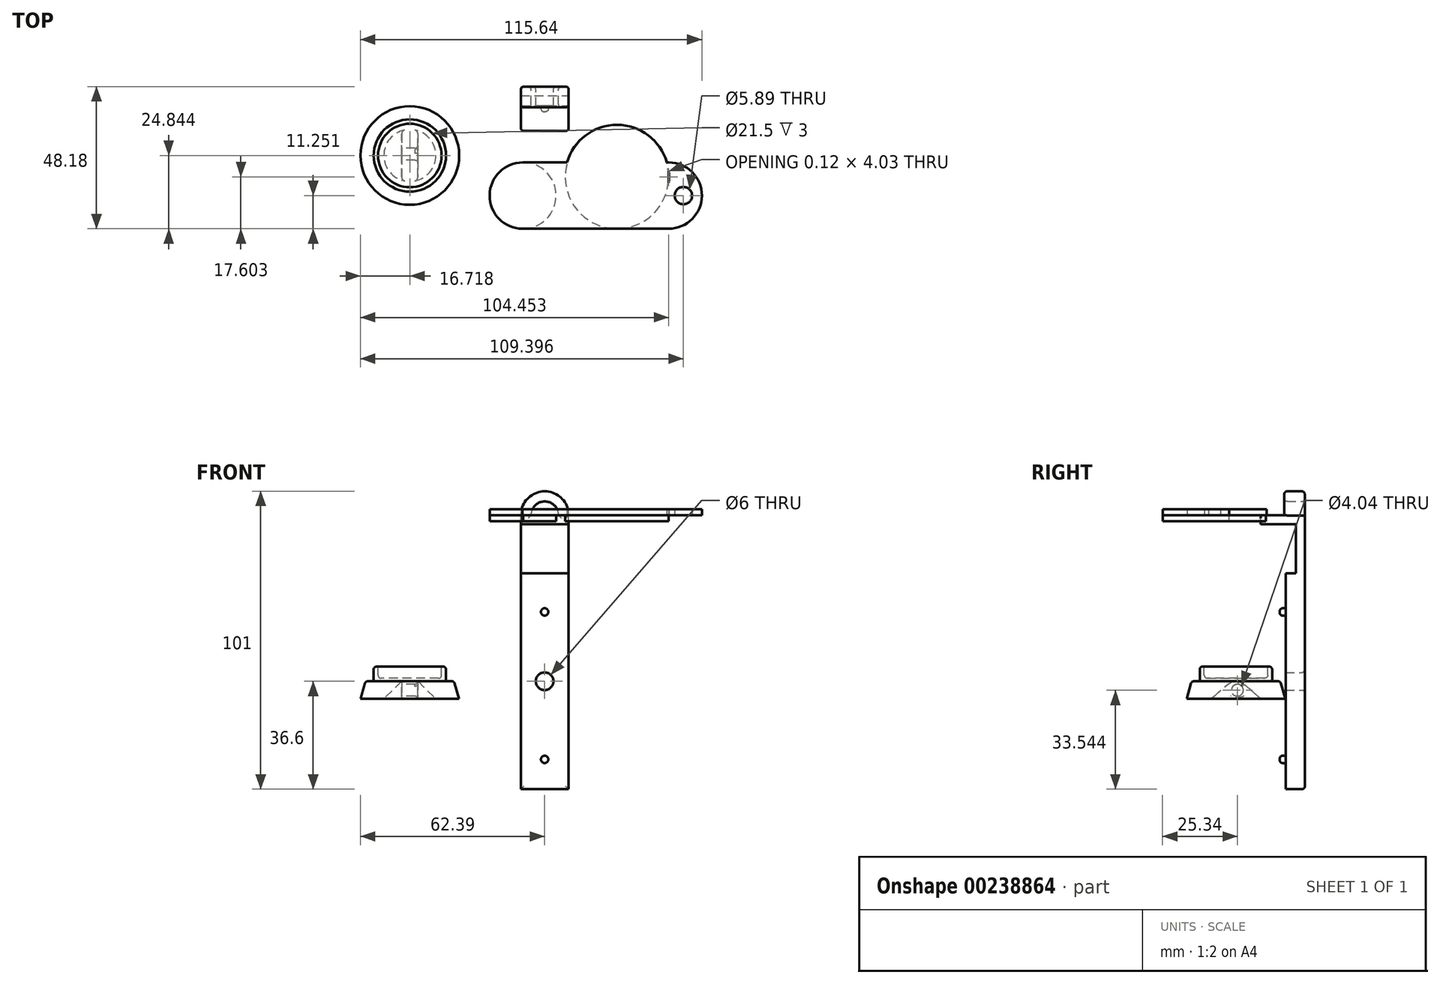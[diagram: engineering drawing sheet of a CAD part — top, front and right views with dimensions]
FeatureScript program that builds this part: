
annotation { "Feature Type Name" : "Feature", "Feature Type Description" : "" }
export const myFeature = defineFeature(function(context is Context, id is Id, definition is map)
    precondition{}
    {
        {
            var Q0;
            Q0=qCreatedBy(makeId("Front.planeOp"),FACE);
            var sketch = newSketch(context, id + "F0", { "sketchPlane" : qUnion([Q0])});
            skCircle(sketch, "E0", {"center": v(0, 0) * mm, "radius": 3 * mm});
            skLineSegment(sketch, "E1", {"start": v(0, 0) * mm, "end": v(0, 36.5) * mm});
            skCircle(sketch, "E2", {"center": v(0, 0) * mm, "radius": 8.06 * mm});
            skLineSegment(sketch, "E3.bottom", {"start": v(-8.06, 0) * mm, "end": v(8.14, 0) * mm});
            skLineSegment(sketch, "E3.top", {"start": v(-8.06, 36.6) * mm, "end": v(8.14, 36.6) * mm});
            skLineSegment(sketch, "E3.left", {"start": v(-8.06, 0) * mm, "end": v(-8.06, 36.6) * mm});
            skLineSegment(sketch, "E3.right", {"start": v(8.14, 0) * mm, "end": v(8.14, 36.6) * mm});
            skLineSegment(sketch, "E4.MirrorCS", {"start": v(8.14, 0) * mm, "end": v(8.14, -36.6) * mm});
            skLineSegment(sketch, "E5.MirrorCS", {"start": v(-8.06, -36.6) * mm, "end": v(8.14, -36.6) * mm});
            skLineSegment(sketch, "E6.MirrorCS", {"start": v(-8.06, 0) * mm, "end": v(-8.06, -36.6) * mm});
            skSolve(sketch);
        }
        {
            var Q0;
            Q0=makeQuery(id+"F0.imprint","IMPRINT",FACE,{"disambiguationData":[TD([[makeQuery(id+"F0.imprint","IMPRINT",EDGE,{"derivedFrom":sQuery(id+"F0.wireOp",EDGE,"E3.top")}),-1.0]])]});
            var Q1;
            {var subQ0=sQuery(id+"F0.wireOp",EDGE,"E1");var subQ1=sQuery(id+"F0.wireOp",EDGE,"E0");var subQ2=makeQuery(id+"F0.imprint","INTERSECT",VERTEX,{"derivedFrom":[subQ1,subQ0]});Q1=makeQuery(id+"F0.imprint","IMPRINT",FACE,{"disambiguationData":[TD([[makeQuery(id+"F0.imprint","IMPRINT",EDGE,{"disambiguationData":[TD([[subQ2,-1.0]])],"derivedFrom":subQ1}),-1.0]])]});}
            var Q2;
            {var subQ0=sQuery(id+"F0.wireOp",EDGE,"E1");var subQ1=sQuery(id+"F0.wireOp",EDGE,"E0");var subQ2=makeQuery(id+"F0.imprint","INTERSECT",VERTEX,{"derivedFrom":[subQ1,subQ0]});Q2=makeQuery(id+"F0.imprint","IMPRINT",FACE,{"disambiguationData":[TD([[makeQuery(id+"F0.imprint","IMPRINT",EDGE,{"disambiguationData":[TD([[subQ2,1.0]])],"derivedFrom":subQ1}),-1.0]])]});}
            var Q3;
            {var subQ0=sQuery(id+"F0.wireOp",EDGE,"E3.bottom");var subQ1=sQuery(id+"F0.wireOp",EDGE,"E0");var subQ2=makeQuery(id+"F0.imprint","INTERSECT",VERTEX,{"disambiguationData":[OD(0.0)],"derivedFrom":[subQ1,subQ0]});Q3=makeQuery(id+"F0.imprint","IMPRINT",FACE,{"disambiguationData":[TD([[makeQuery(id+"F0.imprint","IMPRINT",EDGE,{"disambiguationData":[TD([[subQ2,1.0]])],"derivedFrom":subQ1}),-1.0]])]});}
            var Q4;
            {var subQ0=sQuery(id+"F0.wireOp",EDGE,"E4.MirrorCS");Q4=makeQuery(id+"F0.imprint","IMPRINT",FACE,{"disambiguationData":[TD([[makeQuery(id+"F0.imprint","IMPRINT",EDGE,{"derivedFrom":subQ0}),-1.0]])]});}
            extrude(context, id + "F1", {"entities" : qUnion([Q0, Q1, Q2, Q3, Q4]), "depth" : 3.5 * mm});
        }
        {
            var Q0;
            Q0=makeQuery(id+"F1.opExtrude","CAP_FACE",FACE,{"disambiguationData":[OSD([sQuery(id+"F0.wireOp",EDGE,"E0"),sQuery(id+"F0.wireOp",EDGE,"E2"),sQuery(id+"F0.wireOp",EDGE,"E3.bottom"),sQuery(id+"F0.wireOp",EDGE,"E3.top"),sQuery(id+"F0.wireOp",EDGE,"E3.left"),sQuery(id+"F0.wireOp",EDGE,"E3.right")])],"isStart":false});
            var sketch = newSketch(context, id + "F2", { "sketchPlane" : qUnion([Q0])});
            skLineSegment(sketch, "E7", {"start": v(0, 0) * mm, "end": v(0, 23.5) * mm});
            skCircle(sketch, "E8", {"center": v(0, 23.5) * mm, "radius": 1.25 * mm});
            skLineSegment(sketch, "E9", {"start": v(-5.3, 0) * mm, "end": v(-5.3, -26.5) * mm});
            skCircle(sketch, "E10", {"center": v(0, -26.5) * mm, "radius": 1.24 * mm});
            skSolve(sketch);
        }
        {
            var Q0;
            Q0=makeQuery(id+"F2.imprint","IMPRINT",FACE,{"disambiguationData":[TD([[makeQuery(id+"F2.imprint","IMPRINT",EDGE,{"derivedFrom":sQuery(id+"F2.wireOp",EDGE,"E8")}),1.0]])]});
            var Q1;
            Q1=makeQuery(id+"F2.imprint","IMPRINT",FACE,{"disambiguationData":[TD([[makeQuery(id+"F2.imprint","IMPRINT",EDGE,{"derivedFrom":sQuery(id+"F2.wireOp",EDGE,"E10")}),1.0]])]});
            extrude(context, id + "F3", {"entities" : qUnion([Q0, Q1]), "operationType" : NewBodyOperationType.ADD, "depth" : 2 * mm});
        }
        {
            var Q0;
            Q0=makeQuery(id+"F1.opExtrude","CAP_FACE",FACE,{"disambiguationData":[OSD([sQuery(id+"F0.wireOp",EDGE,"E0"),sQuery(id+"F0.wireOp",EDGE,"E2"),sQuery(id+"F0.wireOp",EDGE,"E3.bottom"),sQuery(id+"F0.wireOp",EDGE,"E3.top"),sQuery(id+"F0.wireOp",EDGE,"E3.left"),sQuery(id+"F0.wireOp",EDGE,"E3.right")])],"isStart":true});
            extrude(context, id + "F4", {"entities" : qUnion([Q0]), "operationType" : NewBodyOperationType.ADD, "depth" : 3 * mm});
        }
        {
            var Q0;
            {var subQ0=sQuery(id+"F0.wireOp",EDGE,"E3.top");Q0=makeQuery(id+"F4.boolean.opBoolean","MERGE",FACE,{"derivedFrom":[makeQuery(id+"F1.opExtrude","SWEPT_FACE",FACE,{"disambiguationData":[OSD([subQ0])]}),makeQuery(id+"F4.opExtrude","SWEPT_FACE",FACE,{"disambiguationData":[OSD([subQ0])]})]});}
            var sketch = newSketch(context, id + "F5", { "sketchPlane" : qUnion([Q0])});
            skLineSegment(sketch, "E11.bottom", {"start": v(-8.06, 3) * mm, "end": v(8.14, 3) * mm});
            skLineSegment(sketch, "E11.top", {"start": v(-8.06, 0) * mm, "end": v(8.14, 0) * mm});
            skLineSegment(sketch, "E11.left", {"start": v(-8.06, 3) * mm, "end": v(-8.06, 0) * mm});
            skLineSegment(sketch, "E11.right", {"start": v(8.14, 3) * mm, "end": v(8.14, 0) * mm});
            skSolve(sketch);
        }
        {
            var Q0;
            Q0=makeQuery(id+"F5.imprint","IMPRINT",FACE,{"disambiguationData":[TD([[makeQuery(id+"F5.imprint","IMPRINT",EDGE,{"derivedFrom":sQuery(id+"F5.wireOp",EDGE,"E11.bottom")}),-1.0]])]});
            extrude(context, id + "F6", {"entities" : qUnion([Q0]), "operationType" : NewBodyOperationType.ADD, "depth" : 16.7 * mm});
        }
        {
            var Q0;
            {var subQ0=sQuery(id+"F0.wireOp",EDGE,"E3.right");Q0=makeQuery(id+"F6.boolean.opBoolean","MERGE",FACE,{"derivedFrom":[makeQuery(id+"F4.boolean.opBoolean","MERGE",FACE,{"derivedFrom":[makeQuery(id+"F1.opExtrude","SWEPT_FACE",FACE,{"disambiguationData":[OSD([subQ0])]}),makeQuery(id+"F4.opExtrude","SWEPT_FACE",FACE,{"disambiguationData":[OSD([subQ0])]})]}),makeQuery(id+"F6.opExtrude","SWEPT_FACE",FACE,{"disambiguationData":[OSD([sQuery(id+"F5.wireOp",EDGE,"E11.right")])]})]});}
            var sketch = newSketch(context, id + "F7", { "sketchPlane" : qUnion([Q0])});
            skLineSegment(sketch, "E12.bottom", {"start": v(3, 53.3) * mm, "end": v(-12, 53.3) * mm});
            skLineSegment(sketch, "E12.top", {"start": v(3, 56.3) * mm, "end": v(-12, 56.3) * mm});
            skLineSegment(sketch, "E12.left", {"start": v(3, 53.3) * mm, "end": v(3, 56.3) * mm});
            skLineSegment(sketch, "E12.right", {"start": v(-12, 53.3) * mm, "end": v(-12, 56.3) * mm});
            skSolve(sketch);
        }
        {
            var Q0;
            Q0=makeQuery(id+"F7.imprint","IMPRINT",FACE,{"disambiguationData":[TD([[makeQuery(id+"F7.imprint","IMPRINT",EDGE,{"derivedFrom":sQuery(id+"F7.wireOp",EDGE,"E12.top")}),1.0]])]});
            extrude(context, id + "F8", {"entities" : qUnion([Q0]), "operationType" : NewBodyOperationType.ADD, "oppositeDirection" : true, "depth" : 16.2 * mm});
        }
        {
            var Q0;
            Q0=makeQuery(id+"F8.boolean.opBoolean","MERGE",FACE,{"derivedFrom":[makeQuery(id+"F6.boolean.opBoolean","MERGE",FACE,{"derivedFrom":[makeQuery(id+"F4.opExtrude","CAP_FACE",FACE,{"disambiguationData":[OSD([sQuery(id+"F0.wireOp",EDGE,"E0"),sQuery(id+"F0.wireOp",EDGE,"E3.top"),sQuery(id+"F0.wireOp",EDGE,"E3.left"),sQuery(id+"F0.wireOp",EDGE,"E3.right"),sQuery(id+"F0.wireOp",EDGE,"E4.MirrorCS"),sQuery(id+"F0.wireOp",EDGE,"E5.MirrorCS"),sQuery(id+"F0.wireOp",EDGE,"E6.MirrorCS")])],"isStart":false}),makeQuery(id+"F6.opExtrude","SWEPT_FACE",FACE,{"disambiguationData":[OSD([sQuery(id+"F5.wireOp",EDGE,"E11.bottom")])]})]}),makeQuery(id+"F8.opExtrude","SWEPT_FACE",FACE,{"disambiguationData":[OSD([sQuery(id+"F7.wireOp",EDGE,"E12.left")])]})]});
            var sketch = newSketch(context, id + "F9", { "sketchPlane" : qUnion([Q0])});
            skCircle(sketch, "E13", {"center": v(-0.04, 56.3) * mm, "radius": 8.1 * mm});
            skCircle(sketch, "E14", {"center": v(-0.04, 56.3) * mm, "radius": 4.66 * mm});
            skSolve(sketch);
        }
        {
            var Q0;
            {var subQ0=sQuery(id+"F7.wireOp",EDGE,"E12.left");var subQ1=makeQuery(id+"F8.opExtrude","CAP_EDGE",EDGE,{"disambiguationData":[OSD([subQ0])],"isStart":false});var subQ9=sQuery(id+"F9.wireOp",EDGE,"E13");var subQ11=makeQuery(id+"F9.imprint","INTERSECT",VERTEX,{"derivedFrom":[subQ1,subQ9]});Q0=makeQuery(id+"F9.imprint","IMPRINT",FACE,{"disambiguationData":[TD([[makeQuery(id+"F9.imprint","IMPRINT",EDGE,{"disambiguationData":[TD([[subQ11,-1.0]])],"derivedFrom":subQ1}),-1.0]])]});}
            extrude(context, id + "F10", {"entities" : qUnion([Q0]), "operationType" : NewBodyOperationType.ADD, "oppositeDirection" : true, "depth" : 7 * mm});
        }
        {
            var Q0;
            Q0=makeQuery(id+"F8.opExtrude","SWEPT_FACE",FACE,{"disambiguationData":[OSD([sQuery(id+"F7.wireOp",EDGE,"E12.top")])]});
            var sketch = newSketch(context, id + "F11", { "sketchPlane" : qUnion([Q0])});
            skCircle(sketch, "E15", {"center": v(24.5, -27.68) * mm, "radius": 17.5 * mm});
            skLineSegment(sketch, "E16", {"start": v(24.5, -45.18) * mm, "end": v(-7.5, -45.18) * mm});
            skCircle(sketch, "E17", {"center": v(-7.38, -33.93) * mm, "radius": 11.25 * mm});
            skPoint(sketch, "E17.second.point", {"position": v(-7.5, -22.68) * mm});
            skPoint(sketch, "E17.third.point", {"position": v(3.87, -33.79) * mm});
            skSolve(sketch);
        }
        {
            var Q0;
            {var subQ0=sQuery(id+"F11.wireOp",EDGE,"E17");var subQ1=sQuery(id+"F11.wireOp",EDGE,"E16");var subQ2=makeQuery(id+"F11.imprint","INTERSECT",VERTEX,{"disambiguationData":[OD(0.0)],"derivedFrom":[subQ1,subQ0]});Q0=makeQuery(id+"F11.imprint","IMPRINT",FACE,{"disambiguationData":[TD([[makeQuery(id+"F11.imprint","IMPRINT",EDGE,{"disambiguationData":[TD([[subQ2,1.0]])],"derivedFrom":subQ1}),-1.0]])]});}
            var Q1;
            Q1=makeQuery(id+"F11.imprint","IMPRINT",FACE,{"disambiguationData":[TD([[makeQuery(id+"F11.imprint","IMPRINT",EDGE,{"derivedFrom":sQuery(id+"F11.wireOp",EDGE,"E15")}),1.0]])]});
            extrude(context, id + "F12", {"entities" : qUnion([Q0, Q1]), "oppositeDirection" : true, "depth" : 2 * mm});
        }
        {
            var Q0;
            Q0=makeQuery(id+"F12.opExtrude","CAP_FACE",FACE,{"disambiguationData":[OSD([sQuery(id+"F11.wireOp",EDGE,"E16"),sQuery(id+"F11.wireOp",EDGE,"E17")])],"isStart":true});
            var sketch = newSketch(context, id + "F13", { "sketchPlane" : qUnion([Q0])});
            skLineSegment(sketch, "E18.bottom", {"start": v(-7.38, -22.68) * mm, "end": v(25.1, -22.68) * mm});
            skLineSegment(sketch, "E18.top", {"start": v(-7.38, -45.18) * mm, "end": v(25.1, -45.18) * mm});
            skLineSegment(sketch, "E18.left", {"start": v(-7.38, -22.68) * mm, "end": v(-7.38, -45.18) * mm});
            skLineSegment(sketch, "E18.right", {"start": v(25.1, -22.68) * mm, "end": v(25.1, -45.18) * mm});
            skCircle(sketch, "E19", {"center": v(24.5, -27.58) * mm, "radius": 17.61 * mm});
            skPoint(sketch, "E19.first.point", {"position": v(22.08, -10.13) * mm});
            skPoint(sketch, "E19.third.point", {"position": v(42.05, -29.2) * mm});
            skLineSegment(sketch, "E20.bottom", {"start": v(25.1, -22.68) * mm, "end": v(42, -22.68) * mm});
            skLineSegment(sketch, "E20.top", {"start": v(25.1, -45.18) * mm, "end": v(42, -45.18) * mm});
            skLineSegment(sketch, "E20.right", {"start": v(42, -22.68) * mm, "end": v(42, -45.18) * mm});
            skArc(sketch, "E21", {"start": v(42, -45.18) * mm, "mid": v(53.25, -33.93) * mm, "end": v(42, -22.68) * mm});
            skCircle(sketch, "E22", {"center": v(47, -33.93) * mm, "radius": 2.94 * mm});
            skSolve(sketch);
        }
        {
            var Q0;
            {var subQ0=sQuery(id+"F13.wireOp",EDGE,"E18.right");Q0=makeQuery(id+"F13.imprint","IMPRINT",FACE,{"disambiguationData":[TD([[makeQuery(id+"F13.imprint","IMPRINT",EDGE,{"derivedFrom":subQ0}),1.0]])]});}
            var Q1;
            {var subQ3=sQuery(id+"F13.wireOp",EDGE,"E19");var subQ5=sQuery(id+"F13.wireOp",EDGE,"E18.top");var subQ7=makeQuery(id+"F13.imprint","INTERSECT",VERTEX,{"derivedFrom":[subQ5,subQ3]});Q1=makeQuery(id+"F13.imprint","IMPRINT",FACE,{"disambiguationData":[TD([[makeQuery(id+"F13.imprint","IMPRINT",EDGE,{"disambiguationData":[TD([[subQ7,1.0]])],"derivedFrom":subQ5}),1.0]])]});}
            var Q2;
            {var subQ3=sQuery(id+"F13.wireOp",EDGE,"E18.left");Q2=makeQuery(id+"F13.imprint","IMPRINT",FACE,{"disambiguationData":[TD([[makeQuery(id+"F13.imprint","IMPRINT",EDGE,{"derivedFrom":subQ3}),1.0]])]});}
            var Q3;
            {var subQ0=sQuery(id+"F13.wireOp",EDGE,"E18.left");Q3=makeQuery(id+"F13.imprint","IMPRINT",FACE,{"disambiguationData":[TD([[makeQuery(id+"F13.imprint","IMPRINT",EDGE,{"derivedFrom":subQ0}),-1.0]])]});}
            var Q4;
            {var subQ3=sQuery(id+"F13.wireOp",EDGE,"E19");var subQ5=sQuery(id+"F13.wireOp",EDGE,"E18.top");var subQ7=makeQuery(id+"F13.imprint","INTERSECT",VERTEX,{"derivedFrom":[subQ5,subQ3]});Q4=makeQuery(id+"F13.imprint","IMPRINT",FACE,{"disambiguationData":[TD([[makeQuery(id+"F13.imprint","IMPRINT",EDGE,{"disambiguationData":[TD([[subQ7,1.0]])],"derivedFrom":subQ5}),1.0]])]});}
            var Q5;
            {var subQ0=sQuery(id+"F13.wireOp",EDGE,"E18.right");Q5=makeQuery(id+"F13.imprint","IMPRINT",FACE,{"disambiguationData":[TD([[makeQuery(id+"F13.imprint","IMPRINT",EDGE,{"derivedFrom":subQ0}),-1.0]])]});}
            var Q6;
            {var subQ1=sQuery(id+"F13.wireOp",EDGE,"E18.bottom");var subQ3=sQuery(id+"F13.wireOp",EDGE,"E19");var subQ4=makeQuery(id+"F13.imprint","INTERSECT",VERTEX,{"derivedFrom":[subQ1,subQ3]});Q6=makeQuery(id+"F13.imprint","IMPRINT",FACE,{"disambiguationData":[TD([[makeQuery(id+"F13.imprint","IMPRINT",EDGE,{"disambiguationData":[TD([[subQ4,1.0]])],"derivedFrom":subQ3}),1.0]])]});}
            var Q7;
            {var subQ0=sQuery(id+"F13.wireOp",EDGE,"E18.right");Q7=makeQuery(id+"F13.imprint","IMPRINT",FACE,{"disambiguationData":[TD([[makeQuery(id+"F13.imprint","IMPRINT",EDGE,{"derivedFrom":subQ0}),1.0]])]});}
            var Q8;
            {var subQ0=sQuery(id+"F13.wireOp",EDGE,"E21");Q8=makeQuery(id+"F13.imprint","IMPRINT",FACE,{"disambiguationData":[TD([[makeQuery(id+"F13.imprint","IMPRINT",EDGE,{"derivedFrom":subQ0}),1.0]])]});}
            var Q9;
            {var subQ0=sQuery(id+"F13.wireOp",EDGE,"E20.top");Q9=makeQuery(id+"F13.imprint","IMPRINT",FACE,{"disambiguationData":[TD([[makeQuery(id+"F13.imprint","IMPRINT",EDGE,{"derivedFrom":subQ0}),1.0]])]});}
            var Q10;
            {var subQ0=sQuery(id+"F13.wireOp",EDGE,"E20.bottom");var subQ1=sQuery(id+"F13.wireOp",EDGE,"E19");var subQ2=makeQuery(id+"F13.imprint","INTERSECT",VERTEX,{"derivedFrom":[subQ1,subQ0]});Q10=makeQuery(id+"F13.imprint","IMPRINT",FACE,{"disambiguationData":[TD([[makeQuery(id+"F13.imprint","IMPRINT",EDGE,{"disambiguationData":[TD([[subQ2,1.0]])],"derivedFrom":subQ1}),-1.0]])]});}
            var Q11;
            {var subQ0=sQuery(id+"F13.wireOp",EDGE,"E20.right");var subQ1=sQuery(id+"F13.wireOp",EDGE,"E19");var subQ2=makeQuery(id+"F13.imprint","INTERSECT",VERTEX,{"disambiguationData":[OD(0.0)],"derivedFrom":[subQ1,subQ0]});Q11=makeQuery(id+"F13.imprint","IMPRINT",FACE,{"disambiguationData":[TD([[makeQuery(id+"F13.imprint","IMPRINT",EDGE,{"disambiguationData":[TD([[subQ2,1.0]])],"derivedFrom":subQ1}),1.0]])]});}
            extrude(context, id + "F14", {"entities" : qUnion([Q0, Q1, Q2, Q3, Q4, Q5, Q6, Q7, Q8, Q9, Q10, Q11]), "depth" : 2 * mm});
        }
        {
            var Q0;
            Q0=makeQuery(id+"F14.opExtrude","CAP_EDGE",EDGE,{"disambiguationData":[OSD([sQuery(id+"F11.wireOp",EDGE,"E16"),sQuery(id+"F13.wireOp",EDGE,"E18.top")])],"isStart":false});
            var Q1;
            Q1=makeQuery(id+"F14.opExtrude","CAP_EDGE",EDGE,{"disambiguationData":[OSD([sQuery(id+"F11.wireOp",EDGE,"E17")])],"isStart":false});
            var Q2;
            Q2=makeQuery(id+"F14.opExtrude","CAP_EDGE",EDGE,{"disambiguationData":[OSD([sQuery(id+"F13.wireOp",EDGE,"E19")])],"isStart":false});
            var Q3;
            Q3=makeQuery(id+"F10.opExtrude","CAP_EDGE",EDGE,{"disambiguationData":[OSD([sQuery(id+"F9.wireOp",EDGE,"E14")])],"isStart":true});
            var Q4;
            Q4=makeQuery(id+"F10.opExtrude","CAP_EDGE",EDGE,{"disambiguationData":[OSD([sQuery(id+"F9.wireOp",EDGE,"E13")])],"isStart":true});
            var Q5;
            Q5=makeQuery(id+"F10.opExtrude","CAP_EDGE",EDGE,{"disambiguationData":[OSD([sQuery(id+"F9.wireOp",EDGE,"E13")])],"isStart":false});
            var Q6;
            Q6=makeQuery(id+"F10.opExtrude","CAP_EDGE",EDGE,{"disambiguationData":[OSD([sQuery(id+"F9.wireOp",EDGE,"E14")])],"isStart":false});
            var Q7;
            Q7=makeQuery(id+"F6.opExtrude","CAP_EDGE",EDGE,{"disambiguationData":[OSD([sQuery(id+"F5.wireOp",EDGE,"E11.top")])],"isStart":false});
            var Q8;
            Q8=makeQuery(id+"F8.opExtrude","CAP_EDGE",EDGE,{"disambiguationData":[OSD([sQuery(id+"F7.wireOp",EDGE,"E12.right")])],"isStart":true});
            var Q9;
            Q9=makeQuery(id+"F8.opExtrude","CAP_EDGE",EDGE,{"disambiguationData":[OSD([sQuery(id+"F7.wireOp",EDGE,"E12.right")])],"isStart":false});
            var Q10;
            Q10=makeQuery(id+"F4.opExtrude","CAP_EDGE",EDGE,{"disambiguationData":[OSD([sQuery(id+"F0.wireOp",EDGE,"E5.MirrorCS")])],"isStart":false});
            var Q11;
            Q11=makeQuery(id+"F8.opExtrude","SWEPT_EDGE",EDGE,{"disambiguationData":[OSD([sQuery(id+"F7.wireOp",EDGE,"E12.top"),sQuery(id+"F7.wireOp",EDGE,"E12.left")])]});
            var Q12;
            Q12=makeQuery(id+"F8.opExtrude","SWEPT_EDGE",EDGE,{"disambiguationData":[OSD([sQuery(id+"F7.wireOp",EDGE,"E12.top"),sQuery(id+"F7.wireOp",EDGE,"E12.right")])]});
            var Q13;
            Q13=makeQuery(id+"F3.opExtrude","CAP_EDGE",EDGE,{"disambiguationData":[OSD([sQuery(id+"F2.wireOp",EDGE,"E8")])],"isStart":false});
            var Q14;
            Q14=makeQuery(id+"F3.opExtrude","CAP_EDGE",EDGE,{"disambiguationData":[OSD([sQuery(id+"F2.wireOp",EDGE,"E10")])],"isStart":false});
            var Q15;
            Q15=makeQuery(id+"F14.opExtrude","CAP_EDGE",EDGE,{"disambiguationData":[OSD([sQuery(id+"F13.wireOp",EDGE,"E22")])],"isStart":false});
            var Q16;
            Q16=makeQuery(id+"F14.opExtrude","CAP_EDGE",EDGE,{"disambiguationData":[OSD([sQuery(id+"F13.wireOp",EDGE,"E22")])],"isStart":true});
            var Q17;
            Q17=makeQuery(id+"F4.opExtrude","CAP_EDGE",EDGE,{"disambiguationData":[OSD([sQuery(id+"F0.wireOp",EDGE,"E0")])],"isStart":false});
            fillet(context, id + "F15", {"entities" : qUnion([Q0, Q1, Q2, Q3, Q4, Q5, Q6, Q7, Q8, Q9, Q10, Q11, Q12, Q13, Q14, Q15, Q16, Q17]), "radius" : 1 * mm, "tangentPropagation" : true, "allowEdgeOverflow" : false});
        }
        {
            var Q0;
            Q0=qCreatedBy(makeId("Top.planeOp"),FACE);
            var sketch = newSketch(context, id + "F16", { "sketchPlane" : qUnion([Q0])});
            skCircle(sketch, "E23", {"center": v(-45.67, -20.34) * mm, "radius": 12.25 * mm});
            skSolve(sketch);
        }
        {
            var Q0;
            Q0=makeQuery(id+"F16.imprint","IMPRINT",FACE,{"disambiguationData":[TD([[makeQuery(id+"F16.imprint","IMPRINT",EDGE,{"derivedFrom":sQuery(id+"F16.wireOp",EDGE,"E23")}),1.0]])]});
            extrude(context, id + "F17", {"entities" : qUnion([Q0]), "depth" : 5 * mm});
        }
        {
            var Q0;
            Q0=makeQuery(id+"F17.opExtrude","CAP_FACE",FACE,{"disambiguationData":[OSD([sQuery(id+"F16.wireOp",EDGE,"E23")])],"isStart":false});
            var sketch = newSketch(context, id + "F18", { "sketchPlane" : qUnion([Q0])});
            skCircle(sketch, "E24", {"center": v(-45.67, -20.34) * mm, "radius": 10.75 * mm});
            skSolve(sketch);
        }
        {
            var Q0;
            Q0=makeQuery(id+"F18.imprint","IMPRINT",FACE,{"disambiguationData":[TD([[makeQuery(id+"F18.imprint","IMPRINT",EDGE,{"derivedFrom":sQuery(id+"F18.wireOp",EDGE,"E24")}),1.0]])]});
            extrude(context, id + "F19", {"entities" : qUnion([Q0]), "operationType" : NewBodyOperationType.REMOVE, "oppositeDirection" : true, "depth" : 4 * mm});
        }
        {
            var Q0;
            Q0=makeQuery(id+"F17.opExtrude","CAP_FACE",FACE,{"disambiguationData":[OSD([sQuery(id+"F16.wireOp",EDGE,"E23")])],"isStart":true});
            var sketch = newSketch(context, id + "F20", { "sketchPlane" : qUnion([Q0])});
            skCircle(sketch, "E25", {"center": v(-45.67, 20.34) * mm, "radius": 15 * mm});
            skSolve(sketch);
        }
        {
            var Q0;
            Q0=makeQuery(id+"F20.imprint","IMPRINT",FACE,{"disambiguationData":[TD([[makeQuery(id+"F20.imprint","IMPRINT",EDGE,{"derivedFrom":makeQuery(id+"F17.opExtrude","CAP_EDGE",EDGE,{"disambiguationData":[OSD([sQuery(id+"F16.wireOp",EDGE,"E23")])],"isStart":true})}),-1.0]])]});
            var Q1;
            Q1=makeQuery(id+"F20.imprint","IMPRINT",FACE,{"disambiguationData":[TD([[makeQuery(id+"F20.imprint","IMPRINT",EDGE,{"derivedFrom":sQuery(id+"F20.wireOp",EDGE,"E25")}),1.0]])]});
            extrude(context, id + "F21", {"entities" : qUnion([Q0, Q1]), "operationType" : NewBodyOperationType.ADD, "depth" : 6 * mm, "hasDraft" : true, "draftAngle" : 16 * degree});
        }
        {
            var Q0;
            Q0=makeQuery(id+"F21.opExtrude","CAP_FACE",FACE,{"disambiguationData":[OSD([sQuery(id+"F20.wireOp",EDGE,"E25")])],"isStart":false});
            var sketch = newSketch(context, id + "F22", { "sketchPlane" : qUnion([Q0])});
            skLineSegment(sketch, "E26", {"start": v(-46, 37.5) * mm, "end": v(-46, 3.5) * mm});
            skCircle(sketch, "E27", {"center": v(-45.67, 20.34) * mm, "radius": 8.8 * mm});
            skSolve(sketch);
        }
        {
            var Q0;
            {var subQ0=sQuery(id+"F22.wireOp",EDGE,"E27");var subQ1=sQuery(id+"F22.wireOp",EDGE,"E26");var subQ2=makeQuery(id+"F22.imprint","INTERSECT",VERTEX,{"disambiguationData":[OD(0.0)],"derivedFrom":[subQ1,subQ0]});Q0=makeQuery(id+"F22.imprint","IMPRINT",FACE,{"disambiguationData":[TD([[makeQuery(id+"F22.imprint","IMPRINT",EDGE,{"disambiguationData":[TD([[subQ2,-1.0]])],"derivedFrom":subQ1}),-1.0]])]});}
            var Q1;
            {var subQ0=sQuery(id+"F22.wireOp",EDGE,"E27");var subQ1=sQuery(id+"F22.wireOp",EDGE,"E26");var subQ2=makeQuery(id+"F22.imprint","INTERSECT",VERTEX,{"disambiguationData":[OD(0.0)],"derivedFrom":[subQ1,subQ0]});Q1=makeQuery(id+"F22.imprint","IMPRINT",FACE,{"disambiguationData":[TD([[makeQuery(id+"F22.imprint","IMPRINT",EDGE,{"disambiguationData":[TD([[subQ2,-1.0]])],"derivedFrom":subQ1}),1.0]])]});}
            extrude(context, id + "F23", {"entities" : qUnion([Q0, Q1]), "operationType" : NewBodyOperationType.REMOVE, "oppositeDirection" : true, "depth" : 6 * mm, "hasDraft" : true, "draftAngle" : 45 * degree, "draftPullDirection" : true});
        }
        {
            var Q0;
            Q0=makeQuery(id+"F21.opExtrude","CAP_FACE",FACE,{"disambiguationData":[OSD([sQuery(id+"F20.wireOp",EDGE,"E25")])],"isStart":false});
            var sketch = newSketch(context, id + "F24", { "sketchPlane" : qUnion([Q0])});
            skLineSegment(sketch, "E28.bottom", {"start": v(-48.43, 10.28) * mm, "end": v(-42.93, 10.28) * mm});
            skLineSegment(sketch, "E28.top", {"start": v(-48.43, 30.38) * mm, "end": v(-42.93, 30.38) * mm});
            skLineSegment(sketch, "E28.left", {"start": v(-48.43, 10.28) * mm, "end": v(-48.43, 30.38) * mm});
            skLineSegment(sketch, "E28.right", {"start": v(-42.93, 10.28) * mm, "end": v(-42.93, 30.38) * mm});
            skSolve(sketch);
        }
        {
            var Q0;
            {var subQ0=sQuery(id+"F24.wireOp",EDGE,"E28.left");var subQ1=makeQuery(id+"F23.boolean.opBoolean","COPY",EDGE,{"derivedFrom":makeQuery(id+"F23.opExtrude","CAP_EDGE",EDGE,{"disambiguationData":[OSD([sQuery(id+"F22.wireOp",EDGE,"E27")])],"isStart":true})});var subQ2=makeQuery(id+"F24.imprint","INTERSECT",VERTEX,{"disambiguationData":[OD(0.0)],"derivedFrom":[subQ1,subQ0]});Q0=makeQuery(id+"F24.imprint","IMPRINT",FACE,{"disambiguationData":[TD([[makeQuery(id+"F24.imprint","IMPRINT",EDGE,{"disambiguationData":[TD([[subQ2,-1.0]])],"derivedFrom":subQ0}),-1.0]])]});}
            extrude(context, id + "F25", {"entities" : qUnion([Q0]), "operationType" : NewBodyOperationType.ADD, "oppositeDirection" : true, "depth" : 6.5 * mm});
        }
        {
            var Q0;
            Q0=makeQuery(id+"F25.opExtrude","SWEPT_FACE",FACE,{"disambiguationData":[OSD([sQuery(id+"F24.wireOp",EDGE,"E28.left")])]});
            var sketch = newSketch(context, id + "F26", { "sketchPlane" : qUnion([Q0])});
            skCircle(sketch, "E29", {"center": v(19.84, -3.06) * mm, "radius": 2.02 * mm});
            skSolve(sketch);
        }
        {
            var Q0;
            Q0=makeQuery(id+"F26.imprint","IMPRINT",FACE,{"disambiguationData":[TD([[makeQuery(id+"F26.imprint","IMPRINT",EDGE,{"derivedFrom":sQuery(id+"F26.wireOp",EDGE,"E29")}),1.0]])]});
            var Q1;
            Q1=sQuery(id+"F26.wireOp",EDGE,"E29");
            extrude(context, id + "F27", {"entities" : qUnion([Q0]), "operationType" : NewBodyOperationType.REMOVE, "surfaceEntities" : qUnion([Q1]), "oppositeDirection" : true, "depth" : 6 * mm});
        }
        {
            var Q0;
            Q0=makeQuery(id+"F19.boolean.opBoolean","COPY",EDGE,{"derivedFrom":makeQuery(id+"F19.opExtrude","CAP_EDGE",EDGE,{"disambiguationData":[OSD([sQuery(id+"F18.wireOp",EDGE,"E24")])],"isStart":false})});
            var Q1;
            Q1=makeQuery(id+"F17.opExtrude","CAP_EDGE",EDGE,{"disambiguationData":[OSD([sQuery(id+"F16.wireOp",EDGE,"E23")])],"isStart":false});
            var Q2;
            Q2=makeQuery(id+"F21.opExtrude","CAP_EDGE",EDGE,{"disambiguationData":[OSD([sQuery(id+"F20.wireOp",EDGE,"E25")])],"isStart":true});
            var Q3;
            Q3=makeQuery(id+"F27.boolean.opBoolean","COPY",EDGE,{"derivedFrom":makeQuery(id+"F27.opExtrude","CAP_EDGE",EDGE,{"disambiguationData":[OSD([sQuery(id+"F26.wireOp",EDGE,"E29")])],"isStart":true})});
            var Q4;
            Q4=makeQuery(id+"F27.boolean.opBoolean","INTERSECT",EDGE,{"derivedFrom":[makeQuery(id+"F25.opExtrude","SWEPT_FACE",FACE,{"disambiguationData":[OSD([sQuery(id+"F24.wireOp",EDGE,"E28.right")])]}),makeQuery(id+"F27.opExtrude","SWEPT_FACE",FACE,{"disambiguationData":[OSD([sQuery(id+"F26.wireOp",EDGE,"E29")])]})]});
            var Q5;
            {var subQ0=sQuery(id+"F22.wireOp",EDGE,"E27");var subQ1=sQuery(id+"F24.wireOp",EDGE,"E28.right");Q5=makeQuery(id+"F25.boolean.opBoolean","SPLIT",EDGE,{"disambiguationData":[TD([makeQuery(id+"F25.opExtrude","SWEPT_FACE",FACE,{"disambiguationData":[OSD([subQ1])]})])],"derivedFrom":makeQuery(id+"F23.boolean.opBoolean","COPY",EDGE,{"derivedFrom":makeQuery(id+"F23.opExtrude","CAP_EDGE",EDGE,{"disambiguationData":[OSD([subQ0])],"isStart":true})})});}
            var Q6;
            {var subQ0=sQuery(id+"F22.wireOp",EDGE,"E27");var subQ1=sQuery(id+"F24.wireOp",EDGE,"E28.left");Q6=makeQuery(id+"F25.boolean.opBoolean","SPLIT",EDGE,{"disambiguationData":[TD([makeQuery(id+"F25.opExtrude","SWEPT_FACE",FACE,{"disambiguationData":[OSD([subQ1])]})])],"derivedFrom":makeQuery(id+"F23.boolean.opBoolean","COPY",EDGE,{"derivedFrom":makeQuery(id+"F23.opExtrude","CAP_EDGE",EDGE,{"disambiguationData":[OSD([subQ0])],"isStart":true})})});}
            var Q7;
            Q7=makeQuery(id+"F25.opExtrude","CAP_EDGE",EDGE,{"disambiguationData":[OSD([sQuery(id+"F24.wireOp",EDGE,"E28.left")])],"isStart":true});
            var Q8;
            Q8=makeQuery(id+"F25.opExtrude","CAP_EDGE",EDGE,{"disambiguationData":[OSD([sQuery(id+"F24.wireOp",EDGE,"E28.right")])],"isStart":true});
            fillet(context, id + "F28", {"entities" : qUnion([Q0, Q1, Q2, Q3, Q4, Q5, Q6, Q7, Q8]), "radius" : 1 * mm, "tangentPropagation" : true, "allowEdgeOverflow" : false});
        }
    });
